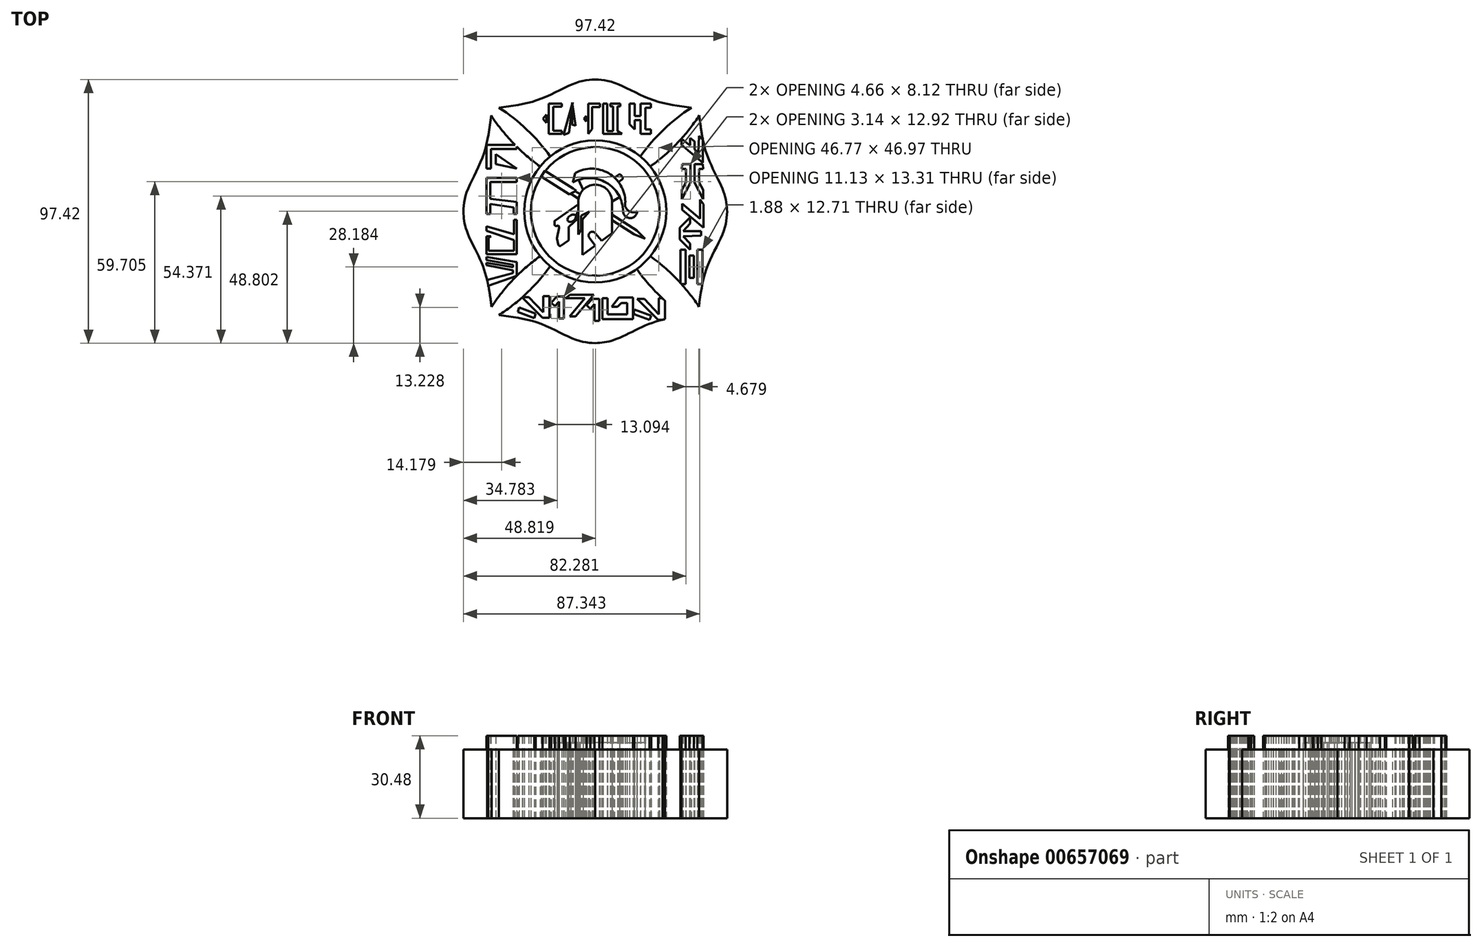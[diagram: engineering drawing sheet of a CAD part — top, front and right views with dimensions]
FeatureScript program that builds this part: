
annotation { "Feature Type Name" : "Feature", "Feature Type Description" : "" }
export const myFeature = defineFeature(function(context is Context, id is Id, definition is map)
    precondition{}
    {
        {
            var Q0;
            Q0=qCreatedBy(makeId("Top.planeOp"),FACE);
            var sketch = newSketch(context, id + "F0", { "sketchPlane" : qUnion([Q0])});
            skCircle(sketch, "E0", {"center": v(0, 0) * mm, "radius": 26.23 * mm});
            skCircle(sketch, "E1", {"center": v(0, 0) * mm, "radius": 23.74 * mm});
            skArc(sketch, "E2", {"start": v(35.51, 38.32) * mm, "mid": v(25.23, 30.18) * mm, "end": v(16.63, 20.3) * mm});
            skArc(sketch, "E3.MirrorCS", {"start": v(38.41, 35.41) * mm, "mid": v(30.25, 25.15) * mm, "end": v(20.34, 16.57) * mm});
            skArc(sketch, "E4.MirrorCS", {"start": v(-35.51, 38.32) * mm, "mid": v(-25.23, 30.18) * mm, "end": v(-16.63, 20.3) * mm});
            skArc(sketch, "E5.MirrorCS", {"start": v(-38.41, 35.41) * mm, "mid": v(-30.25, 25.15) * mm, "end": v(-20.34, 16.57) * mm});
            skArc(sketch, "E6.MirrorCS", {"start": v(-35.51, -38.32) * mm, "mid": v(-25.23, -30.18) * mm, "end": v(-16.63, -20.3) * mm});
            skArc(sketch, "E7.MirrorCS", {"start": v(-38.41, -35.41) * mm, "mid": v(-30.25, -25.15) * mm, "end": v(-20.34, -16.57) * mm});
            skArc(sketch, "E8.MirrorCS", {"start": v(38.41, -35.41) * mm, "mid": v(30.25, -25.15) * mm, "end": v(20.34, -16.57) * mm});
            skFitSpline(sketch, "E9", {"points": [v(-35.51, 38.32) * mm, v(-20.45, 41.42) * mm, v(-6.98, 47.51) * mm, v(0, 48.72) * mm], "startDerivative": vector(40.3, 5.04) * mm, "endDerivative": vector(25.56, 1.65) * mm});
            skFitSpline(sketch, "E10.MirrorCS", {"points": [v(35.51, 38.32) * mm, v(20.45, 41.42) * mm, v(6.98, 47.51) * mm, v(0, 48.72) * mm], "startDerivative": vector(-40.3, 5.04) * mm, "endDerivative": vector(-25.56, 1.65) * mm});
            skFitSpline(sketch, "E11.MirrorCS", {"points": [v(38.41, 35.41) * mm, v(41.47, 20.34) * mm, v(47.53, 6.86) * mm, v(48.72, -0.14) * mm], "startDerivative": vector(4.94, -40.31) * mm, "endDerivative": vector(1.58, -25.56) * mm});
            skFitSpline(sketch, "E12.MirrorCS", {"points": [v(38.23, -35.61) * mm, v(41.37, -20.55) * mm, v(47.5, -7.1) * mm, v(48.72, -0.12) * mm], "startDerivative": vector(5.15, 40.29) * mm, "endDerivative": vector(1.72, 25.55) * mm});
            skArc(sketch, "E13.MirrorCS", {"start": v(34.27, -39.56) * mm, "mid": v(24, -31.4) * mm, "end": v(15.43, -21.48) * mm});
            skFitSpline(sketch, "E14.MirrorCS", {"points": [v(35.51, -38.32) * mm, v(20.45, -41.42) * mm, v(6.98, -47.51) * mm, v(0, -48.72) * mm], "startDerivative": vector(-40.3, -5.04) * mm, "endDerivative": vector(-25.56, -1.65) * mm});
            skFitSpline(sketch, "E15.MirrorCS", {"points": [v(-35.51, -38.32) * mm, v(-20.45, -41.42) * mm, v(-6.98, -47.51) * mm, v(0, -48.72) * mm], "startDerivative": vector(40.3, -5.04) * mm, "endDerivative": vector(25.56, -1.65) * mm});
            skFitSpline(sketch, "E16.MirrorCS", {"points": [v(-38.23, -35.61) * mm, v(-41.37, -20.55) * mm, v(-47.5, -7.1) * mm, v(-48.72, -0.12) * mm], "startDerivative": vector(-5.15, 40.29) * mm, "endDerivative": vector(-1.72, 25.55) * mm});
            skFitSpline(sketch, "E17.MirrorCS", {"points": [v(-38.41, 35.41) * mm, v(-41.47, 20.34) * mm, v(-47.53, 6.86) * mm, v(-48.72, -0.14) * mm], "startDerivative": vector(-4.94, -40.31) * mm, "endDerivative": vector(-1.58, -25.56) * mm});
            skLineSegment(sketch, "E18.left", {"start": v(-6.25, 3.57) * mm, "end": v(-6.25, -8.57) * mm});
            skLineSegment(sketch, "E18.right", {"start": v(6.25, 3.57) * mm, "end": v(6.25, -8.06) * mm});
            skPoint(sketch, "E18.middle", {"position": v(0, -8.06) * mm});
            skArc(sketch, "E19", {"start": v(6.25, 3.57) * mm, "mid": v(0, 9.82) * mm, "end": v(-6.25, 3.57) * mm});
            skLineSegment(sketch, "E20", {"start": v(-4.67, -16.13) * mm, "end": v(0, -12.68) * mm});
            skLineSegment(sketch, "E21", {"start": v(2.37, -10.93) * mm, "end": v(0, -8.06) * mm});
            skLineSegment(sketch, "E22", {"start": v(0, -12.68) * mm, "end": v(-2.14, -9.78) * mm});
            skArc(sketch, "E23", {"start": v(0, -8.06) * mm, "mid": v(-1.93, -7.85) * mm, "end": v(-2.14, -9.78) * mm});
            skPoint(sketch, "E23.third.point", {"position": v(0, -9.78) * mm});
            skLineSegment(sketch, "E24.trimOffspring", {"start": v(2.37, -10.93) * mm, "end": v(6.25, -8.06) * mm});
            skPoint(sketch, "E18.top.end.orphan", {"position": v(6.25, -19.7) * mm});
            skPoint(sketch, "E25.orphan", {"position": v(-6.25, -19.7) * mm});
            skArc(sketch, "E26", {"start": v(11.12, 3.49) * mm, "mid": v(4.91, 14.1) * mm, "end": v(-7.38, 14.17) * mm});
            skArc(sketch, "E27", {"start": v(10.28, 0.03) * mm, "mid": v(4.07, 10.64) * mm, "end": v(-8.22, 10.7) * mm});
            skLineSegment(sketch, "E28", {"start": v(-8.22, 10.7) * mm, "end": v(-7.38, 14.17) * mm});
            skArc(sketch, "E29", {"start": v(11.12, 3.49) * mm, "mid": v(12.15, 0.3) * mm, "end": v(15.48, 0.03) * mm});
            skArc(sketch, "E30", {"start": v(10.28, 0.03) * mm, "mid": v(12.88, -2.5) * mm, "end": v(15.48, 0.03) * mm});
            skLineSegment(sketch, "E31", {"start": v(15.43, -21.48) * mm, "end": v(15.3, -21.3) * mm});
            skLineSegment(sketch, "E32", {"start": v(-4.67, -16.13) * mm, "end": v(-4.67, -2.97) * mm});
            skLineSegment(sketch, "E33", {"start": v(-4.67, -2.97) * mm, "end": v(-2.14, -0.12) * mm});
            skLineSegment(sketch, "E34", {"start": v(-2.14, -0.12) * mm, "end": v(-5.26, -1.55) * mm});
            skPoint(sketch, "E34.endSnap0", {"position": v(-3.4, -1.55) * mm});
            skLineSegment(sketch, "E35", {"start": v(-5.26, -1.55) * mm, "end": v(-5.26, -6.86) * mm});
            skPoint(sketch, "E35.endSnap0", {"position": v(-6.25, -6.86) * mm});
            skLineSegment(sketch, "E36", {"start": v(-5.26, -6.86) * mm, "end": v(-6.25, -8.57) * mm});
            skPoint(sketch, "E37.orphan", {"position": v(-6.25, -17.3) * mm});
            skLineSegment(sketch, "E38", {"start": v(-4.46, 7.95) * mm, "end": v(-6.14, 11.64) * mm});
            skLineSegment(sketch, "E39", {"start": v(6.25, 3.57) * mm, "end": v(9.04, 5.3) * mm});
            skLineSegment(sketch, "E40.bottom", {"start": v(-12.4, 39.78) * mm, "end": v(-17.13, 39.78) * mm});
            skLineSegment(sketch, "E40.top", {"start": v(-12.4, 38.6) * mm, "end": v(-15.49, 38.6) * mm});
            skLineSegment(sketch, "E40.left", {"start": v(-12.4, 39.78) * mm, "end": v(-12.4, 38.6) * mm});
            skLineSegment(sketch, "E40.right", {"start": v(-17.13, 39.78) * mm, "end": v(-17.13, 38.6) * mm});
            skLineSegment(sketch, "E41.bottom", {"start": v(-17.13, 39.78) * mm, "end": v(-15.49, 39.78) * mm});
            skLineSegment(sketch, "E41.left", {"start": v(-17.13, 39.78) * mm, "end": v(-17.13, 34.21) * mm});
            skLineSegment(sketch, "E41.right", {"start": v(-15.49, 38.6) * mm, "end": v(-15.49, 34.21) * mm});
            skLineSegment(sketch, "E42.bottom", {"start": v(-2.52, 39.78) * mm, "end": v(-1.13, 39.78) * mm});
            skLineSegment(sketch, "E42.left", {"start": v(-2.52, 39.78) * mm, "end": v(-2.52, 34.21) * mm});
            skLineSegment(sketch, "E42.right", {"start": v(-1.13, 38.54) * mm, "end": v(-1.13, 34.21) * mm});
            skLineSegment(sketch, "E43.bottom", {"start": v(-2.52, 39.78) * mm, "end": v(1.82, 39.78) * mm});
            skLineSegment(sketch, "E43.top", {"start": v(-1.13, 38.54) * mm, "end": v(1.82, 38.54) * mm});
            skLineSegment(sketch, "E43.left", {"start": v(-2.52, 39.78) * mm, "end": v(-2.52, 38.54) * mm});
            skLineSegment(sketch, "E43.right", {"start": v(1.82, 39.78) * mm, "end": v(1.82, 38.54) * mm});
            skLineSegment(sketch, "E44", {"start": v(-8.28, 40.2) * mm, "end": v(-8.4, 39.75) * mm});
            skLineSegment(sketch, "E45", {"start": v(-11.7, 28.2) * mm, "end": v(-9.65, 28.98) * mm});
            skLineSegment(sketch, "E46", {"start": v(-9.65, 28.98) * mm, "end": v(-8.48, 38.58) * mm});
            skLineSegment(sketch, "E47", {"start": v(-8.48, 40.2) * mm, "end": v(-8.48, 39.51) * mm});
            skLineSegment(sketch, "E48", {"start": v(-8.48, 32.05) * mm, "end": v(-7.25, 31.7) * mm});
            skLineSegment(sketch, "E49", {"start": v(-7.25, 31.7) * mm, "end": v(-8.37, 39.46) * mm});
            skLineSegment(sketch, "E50.MirrorCS", {"start": v(-12.4, 28.65) * mm, "end": v(-17.13, 28.65) * mm});
            skLineSegment(sketch, "E51.MirrorCS", {"start": v(-12.4, 29.82) * mm, "end": v(-15.49, 29.82) * mm});
            skLineSegment(sketch, "E52.MirrorCS", {"start": v(-12.4, 28.65) * mm, "end": v(-12.4, 29.82) * mm});
            skLineSegment(sketch, "E53.MirrorCS", {"start": v(-17.13, 28.65) * mm, "end": v(-17.13, 34.21) * mm});
            skLineSegment(sketch, "E54.MirrorCS", {"start": v(-15.49, 29.82) * mm, "end": v(-15.49, 34.21) * mm});
            skLineSegment(sketch, "E55.MirrorCS", {"start": v(-2.52, 28.65) * mm, "end": v(-2.52, 34.21) * mm});
            skLineSegment(sketch, "E56.MirrorCS", {"start": v(-1.13, 30.44) * mm, "end": v(-1.13, 34.21) * mm});
            skLineSegment(sketch, "E57", {"start": v(-2.52, 28.65) * mm, "end": v(-1.13, 30.44) * mm});
            skPoint(sketch, "E58.orphan", {"position": v(-1.13, 28.65) * mm});
            skPoint(sketch, "E59.orphan", {"position": v(10.7, 28.65) * mm});
            skPoint(sketch, "E60.orphan", {"position": v(10.28, 29.44) * mm});
            skLineSegment(sketch, "E61", {"start": v(-3.29, 35.2) * mm, "end": v(-3.29, 34.21) * mm});
            skPoint(sketch, "E61.endSnap0", {"position": v(-18.03, 34.21) * mm});
            skLineSegment(sketch, "E62", {"start": v(-4.27, 34.21) * mm, "end": v(-3.29, 35.2) * mm});
            skLineSegment(sketch, "E63.MirrorCS", {"start": v(-3.29, 33.23) * mm, "end": v(-3.29, 34.21) * mm});
            skLineSegment(sketch, "E64.MirrorCS", {"start": v(-4.27, 34.21) * mm, "end": v(-3.29, 33.23) * mm});
            skLineSegment(sketch, "E65", {"start": v(-18.03, 35.71) * mm, "end": v(-19.33, 34.21) * mm});
            skLineSegment(sketch, "E66", {"start": v(-18.03, 34.21) * mm, "end": v(-18.03, 35.71) * mm});
            skLineSegment(sketch, "E67", {"start": v(-18.03, 34.21) * mm, "end": v(-18.03, 32.71) * mm});
            skLineSegment(sketch, "E68", {"start": v(-18.03, 32.71) * mm, "end": v(-19.33, 34.21) * mm});
            skLineSegment(sketch, "E69.bottom", {"start": v(2.96, 39.78) * mm, "end": v(4.44, 39.78) * mm});
            skLineSegment(sketch, "E69.top", {"start": v(2.96, 28.65) * mm, "end": v(4.44, 28.65) * mm});
            skLineSegment(sketch, "E69.left", {"start": v(2.96, 39.78) * mm, "end": v(2.96, 28.65) * mm});
            skLineSegment(sketch, "E69.right", {"start": v(4.44, 39.78) * mm, "end": v(4.44, 29.7) * mm});
            skLineSegment(sketch, "E70.bottom", {"start": v(2.96, 28.65) * mm, "end": v(8.18, 28.65) * mm});
            skLineSegment(sketch, "E70.top", {"start": v(4.44, 29.7) * mm, "end": v(6.61, 29.7) * mm});
            skLineSegment(sketch, "E70.left", {"start": v(2.96, 28.65) * mm, "end": v(2.96, 29.7) * mm});
            skLineSegment(sketch, "E71.bottom", {"start": v(8.18, 28.65) * mm, "end": v(6.61, 28.65) * mm});
            skLineSegment(sketch, "E71.top", {"start": v(8.18, 39.78) * mm, "end": v(6.61, 39.78) * mm});
            skLineSegment(sketch, "E71.left", {"start": v(8.18, 29.7) * mm, "end": v(8.18, 38.83) * mm});
            skLineSegment(sketch, "E71.right", {"start": v(6.61, 29.7) * mm, "end": v(6.61, 38.83) * mm});
            skLineSegment(sketch, "E72.bottom", {"start": v(5.53, 39.78) * mm, "end": v(9.3, 39.78) * mm});
            skLineSegment(sketch, "E72.top", {"start": v(5.53, 38.83) * mm, "end": v(6.61, 38.83) * mm});
            skLineSegment(sketch, "E72.left", {"start": v(5.53, 39.78) * mm, "end": v(5.53, 38.83) * mm});
            skLineSegment(sketch, "E72.right", {"start": v(9.3, 39.78) * mm, "end": v(9.3, 38.83) * mm});
            skLineSegment(sketch, "E73", {"start": v(8.18, 29.7) * mm, "end": v(9.87, 28.65) * mm});
            skLineSegment(sketch, "E74", {"start": v(9.87, 28.65) * mm, "end": v(8.18, 28.65) * mm});
            skLineSegment(sketch, "E75.trimOffspring", {"start": v(8.18, 38.83) * mm, "end": v(9.3, 38.83) * mm});
            skLineSegment(sketch, "E76", {"start": v(12.66, 39.78) * mm, "end": v(14.62, 39.78) * mm});
            skLineSegment(sketch, "E77.left", {"start": v(12.66, 39.78) * mm, "end": v(12.66, 32.13) * mm});
            skLineSegment(sketch, "E77.right", {"start": v(14.62, 39.78) * mm, "end": v(14.62, 35.22) * mm});
            skLineSegment(sketch, "E78.bottom", {"start": v(14.62, 35.22) * mm, "end": v(16.76, 35.22) * mm});
            skLineSegment(sketch, "E78.top", {"start": v(14.62, 33.67) * mm, "end": v(16.76, 33.67) * mm});
            skLineSegment(sketch, "E78.left", {"start": v(12.66, 35.22) * mm, "end": v(12.66, 33.67) * mm});
            skLineSegment(sketch, "E79.bottom", {"start": v(16.76, 39.78) * mm, "end": v(18.48, 39.78) * mm});
            skLineSegment(sketch, "E79.top", {"start": v(16.76, 28.65) * mm, "end": v(18.48, 28.65) * mm});
            skLineSegment(sketch, "E79.left", {"start": v(16.76, 39.78) * mm, "end": v(16.76, 35.22) * mm});
            skLineSegment(sketch, "E79.right", {"start": v(18.48, 38.24) * mm, "end": v(18.48, 30.3) * mm});
            skLineSegment(sketch, "E80.bottom", {"start": v(16.76, 39.78) * mm, "end": v(20.61, 39.78) * mm});
            skLineSegment(sketch, "E80.top", {"start": v(18.48, 38.24) * mm, "end": v(20.61, 38.24) * mm});
            skLineSegment(sketch, "E80.left", {"start": v(16.76, 39.78) * mm, "end": v(16.76, 38.24) * mm});
            skLineSegment(sketch, "E80.right", {"start": v(20.61, 39.78) * mm, "end": v(20.61, 38.24) * mm});
            skLineSegment(sketch, "E81.bottom", {"start": v(16.76, 28.65) * mm, "end": v(20.61, 28.65) * mm});
            skLineSegment(sketch, "E81.top", {"start": v(18.48, 30.3) * mm, "end": v(20.61, 30.3) * mm});
            skLineSegment(sketch, "E81.left", {"start": v(16.76, 28.65) * mm, "end": v(16.76, 30.3) * mm});
            skLineSegment(sketch, "E81.right", {"start": v(20.61, 28.65) * mm, "end": v(20.61, 30.3) * mm});
            skLineSegment(sketch, "E82.trimOffspring", {"start": v(18.48, 28.65) * mm, "end": v(20.61, 28.65) * mm});
            skLineSegment(sketch, "E83", {"start": v(12.66, 32.13) * mm, "end": v(14.62, 30.23) * mm});
            skLineSegment(sketch, "E84.trimOffspring", {"start": v(16.76, 33.67) * mm, "end": v(16.76, 28.65) * mm});
            skLineSegment(sketch, "E85.trimOffspring", {"start": v(14.62, 33.67) * mm, "end": v(14.62, 30.23) * mm});
            skLineSegment(sketch, "E86.trimOffspring", {"start": v(-8.4, 39.75) * mm, "end": v(-8.48, 40.2) * mm});
            skLineSegment(sketch, "E87.trimOffspring", {"start": v(-8.48, 39.51) * mm, "end": v(-11.7, 28.2) * mm});
            skLineSegment(sketch, "E88.trimOffspring", {"start": v(-8.37, 39.46) * mm, "end": v(-8.28, 40.2) * mm});
            skLineSegment(sketch, "E89.trimOffspring", {"start": v(-8.48, 38.58) * mm, "end": v(-8.48, 32.05) * mm});
            skLineSegment(sketch, "E90", {"start": v(-28.97, -18.8) * mm, "end": v(-40.1, -16.82) * mm});
            skLineSegment(sketch, "E91", {"start": v(-40.1, -16.82) * mm, "end": v(-40.1, -18.04) * mm});
            skLineSegment(sketch, "E92", {"start": v(-40.1, -18.04) * mm, "end": v(-30.4, -19.76) * mm});
            skLineSegment(sketch, "E93", {"start": v(-30.4, -19.76) * mm, "end": v(-30.4, -20.72) * mm});
            skLineSegment(sketch, "E94", {"start": v(-30.4, -20.72) * mm, "end": v(-40.1, -19) * mm});
            skLineSegment(sketch, "E95", {"start": v(-40.1, -19) * mm, "end": v(-40.1, -19.9) * mm});
            skLineSegment(sketch, "E96", {"start": v(-40.1, -19.9) * mm, "end": v(-30.32, -21.8) * mm});
            skLineSegment(sketch, "E97", {"start": v(-30.32, -21.8) * mm, "end": v(-30.32, -22.87) * mm});
            skLineSegment(sketch, "E98", {"start": v(-30.32, -22.87) * mm, "end": v(-40.1, -25.47) * mm});
            skLineSegment(sketch, "E99", {"start": v(-40.1, -25.47) * mm, "end": v(-40.1, -27.73) * mm});
            skLineSegment(sketch, "E100", {"start": v(-40.1, -27.73) * mm, "end": v(-28.97, -23.85) * mm});
            skLineSegment(sketch, "E101", {"start": v(-28.97, -23.85) * mm, "end": v(-28.97, -18.8) * mm});
            skLineSegment(sketch, "E102.bottom", {"start": v(-40.1, -15.83) * mm, "end": v(-40.1, -14.56) * mm});
            skLineSegment(sketch, "E102.left", {"start": v(-40.1, -15.83) * mm, "end": v(-28.97, -15.83) * mm});
            skLineSegment(sketch, "E102.right", {"start": v(-39.41, -14.56) * mm, "end": v(-30.02, -14.56) * mm});
            skLineSegment(sketch, "E103.bottom", {"start": v(-28.97, -15.83) * mm, "end": v(-28.97, -3.12) * mm});
            skLineSegment(sketch, "E103.top", {"start": v(-30.02, -14.56) * mm, "end": v(-30.02, -10.64) * mm});
            skLineSegment(sketch, "E103.left", {"start": v(-28.97, -15.83) * mm, "end": v(-30.02, -15.83) * mm});
            skLineSegment(sketch, "E103.right", {"start": v(-28.97, -3.12) * mm, "end": v(-30.02, -3.12) * mm});
            skLineSegment(sketch, "E104.left", {"start": v(-38.1, -6.34) * mm, "end": v(-38.11, -6.34) * mm});
            skLineSegment(sketch, "E104.right", {"start": v(-38.1, -5.52) * mm, "end": v(-38.11, -5.52) * mm});
            skLineSegment(sketch, "E105.bottom", {"start": v(-40.1, -15.83) * mm, "end": v(-40.1, -9.27) * mm});
            skLineSegment(sketch, "E105.top", {"start": v(-39.41, -14.56) * mm, "end": v(-39.41, -9.91) * mm});
            skLineSegment(sketch, "E105.left", {"start": v(-40.1, -15.83) * mm, "end": v(-39.41, -15.83) * mm});
            skLineSegment(sketch, "E105.right", {"start": v(-40.1, -9.27) * mm, "end": v(-39.41, -9.27) * mm});
            skLineSegment(sketch, "E106", {"start": v(-40.1, -9.27) * mm, "end": v(-38.43, -9.27) * mm});
            skPoint(sketch, "E106.endSnap0", {"position": v(-39.75, -9.27) * mm});
            skLineSegment(sketch, "E107", {"start": v(-38.43, -9.27) * mm, "end": v(-39.41, -9.91) * mm});
            skLineSegment(sketch, "E108", {"start": v(-30.02, -10.64) * mm, "end": v(-40.1, -7.24) * mm});
            skLineSegment(sketch, "E109", {"start": v(-40.1, -7.24) * mm, "end": v(-40.1, -5.52) * mm});
            skLineSegment(sketch, "E110", {"start": v(-40.1, -5.52) * mm, "end": v(-30.02, -8.5) * mm});
            skLineSegment(sketch, "E111.bottom", {"start": v(-28.97, -0.92) * mm, "end": v(-28.97, 3.44) * mm});
            skLineSegment(sketch, "E111.top", {"start": v(-30.13, -0.92) * mm, "end": v(-30.13, 1.44) * mm});
            skLineSegment(sketch, "E111.left", {"start": v(-28.97, -0.92) * mm, "end": v(-30.13, -0.92) * mm});
            skLineSegment(sketch, "E111.right", {"start": v(-28.97, 3.44) * mm, "end": v(-30.13, 3.44) * mm});
            skLineSegment(sketch, "E112", {"start": v(-30.13, 1.44) * mm, "end": v(-38.78, 2.72) * mm});
            skLineSegment(sketch, "E113", {"start": v(-40.1, 2.92) * mm, "end": v(-40.1, 4.72) * mm});
            skLineSegment(sketch, "E114", {"start": v(-38.78, 4.57) * mm, "end": v(-28.97, 3.44) * mm});
            skLineSegment(sketch, "E115.bottom", {"start": v(-40.1, -1) * mm, "end": v(-40.1, 12.32) * mm});
            skLineSegment(sketch, "E115.top", {"start": v(-38.78, -1) * mm, "end": v(-38.78, 2.72) * mm});
            skLineSegment(sketch, "E115.left", {"start": v(-40.1, -1) * mm, "end": v(-38.78, -1) * mm});
            skLineSegment(sketch, "E115.right", {"start": v(-40.1, 12.32) * mm, "end": v(-38.78, 12.32) * mm});
            skLineSegment(sketch, "E116.bottom", {"start": v(-40.1, 12.32) * mm, "end": v(-40.1, 10.89) * mm});
            skLineSegment(sketch, "E116.top", {"start": v(-28.97, 12.32) * mm, "end": v(-28.97, 10.89) * mm});
            skLineSegment(sketch, "E116.left", {"start": v(-40.1, 12.32) * mm, "end": v(-28.97, 12.32) * mm});
            skLineSegment(sketch, "E116.right", {"start": v(-38.78, 10.89) * mm, "end": v(-28.97, 10.89) * mm});
            skLineSegment(sketch, "E117", {"start": v(-40.1, 15.79) * mm, "end": v(-40.1, 24.5) * mm});
            skLineSegment(sketch, "E118.top", {"start": v(-38.46, 15.79) * mm, "end": v(-38.46, 22.98) * mm});
            skLineSegment(sketch, "E118.left", {"start": v(-40.1, 15.79) * mm, "end": v(-38.46, 15.79) * mm});
            skLineSegment(sketch, "E118.right", {"start": v(-40.1, 24.5) * mm, "end": v(-38.46, 24.5) * mm});
            skLineSegment(sketch, "E119.bottom", {"start": v(-40.1, 24.5) * mm, "end": v(-40.1, 22.98) * mm});
            skLineSegment(sketch, "E119.top", {"start": v(-29, 24.5) * mm, "end": v(-29, 22.98) * mm});
            skLineSegment(sketch, "E119.left", {"start": v(-40.1, 24.5) * mm, "end": v(-29, 24.5) * mm});
            skLineSegment(sketch, "E119.right", {"start": v(-38.46, 22.98) * mm, "end": v(-29, 22.98) * mm});
            skLineSegment(sketch, "E120", {"start": v(-28.97, 15.79) * mm, "end": v(-36.7, 17.48) * mm});
            skLineSegment(sketch, "E121", {"start": v(-36.7, 17.48) * mm, "end": v(-36.7, 21.15) * mm});
            skLineSegment(sketch, "E122", {"start": v(-36.7, 21.15) * mm, "end": v(-28.97, 15.79) * mm});
            skLineSegment(sketch, "E123.trimOffspring", {"start": v(-38.78, 4.57) * mm, "end": v(-38.78, 10.89) * mm});
            skLineSegment(sketch, "E124.trimOffspring", {"start": v(-30.02, -8.5) * mm, "end": v(-30.02, -3.12) * mm});
            skPoint(sketch, "E125.orphan", {"position": v(-40.1, -23.85) * mm});
            skPoint(sketch, "E126.orphan", {"position": v(-28.97, 1.26) * mm});
            skLineSegment(sketch, "E127.bottom", {"start": v(-19.94, 12.89) * mm, "end": v(-9.54, 6.25) * mm});
            skLineSegment(sketch, "E127.top", {"start": v(-18.56, 15.04) * mm, "end": v(-8.17, 8.4) * mm});
            skLineSegment(sketch, "E127.left", {"start": v(-19.94, 12.89) * mm, "end": v(-18.56, 15.04) * mm});
            skLineSegment(sketch, "E127.right", {"start": v(-9.54, 6.25) * mm, "end": v(-8.17, 8.4) * mm});
            skLineSegment(sketch, "E128", {"start": v(-5.9, 6.52) * mm, "end": v(-5.6, 6.34) * mm});
            skLineSegment(sketch, "E129", {"start": v(-7.93, 5.76) * mm, "end": v(-6.16, 4.63) * mm});
            skLineSegment(sketch, "E130", {"start": v(14.39, -8.5) * mm, "end": v(18.41, -10.1) * mm});
            skPoint(sketch, "E130.endSnap0", {"position": v(-81.83, -16.44) * mm});
            skLineSegment(sketch, "E131", {"start": v(18.41, -10.1) * mm, "end": v(15.32, -7.03) * mm});
            skLineSegment(sketch, "E132.0", {"start": v(14.39, -8.5) * mm, "end": v(15.32, -7.03) * mm, "construction": true});
            skLineSegment(sketch, "E133.trimOffspring", {"start": v(6.25, -1.24) * mm, "end": v(15.32, -7.03) * mm});
            skLineSegment(sketch, "E134.trimOffspring", {"start": v(6.25, -3.3) * mm, "end": v(14.39, -8.5) * mm});
            skLineSegment(sketch, "E135", {"start": v(-9.54, 6.25) * mm, "end": v(-7.04, 7.6) * mm});
            skPoint(sketch, "E135.endSnap0", {"position": v(-7.04, 5.2) * mm});
            skLineSegment(sketch, "E136", {"start": v(-7.04, 7.6) * mm, "end": v(-8.17, 8.4) * mm});
            skLineSegment(sketch, "E137", {"start": v(-5.9, 6.52) * mm, "end": v(-7.34, 7.44) * mm});
            skLineSegment(sketch, "E138", {"start": v(-7.93, 5.76) * mm, "end": v(-9.08, 6.5) * mm});
            skLineSegment(sketch, "E139", {"start": v(-9.76, -10.38) * mm, "end": v(-9.76, -5.95) * mm});
            skLineSegment(sketch, "E140", {"start": v(-9.56, -5.5) * mm, "end": v(-6.53, -2.75) * mm});
            skLineSegment(sketch, "E141", {"start": v(-6.35, -2.14) * mm, "end": v(-6.69, -0.96) * mm});
            skLineSegment(sketch, "E142", {"start": v(-6.46, -0.3) * mm, "end": v(-6.25, -0.16) * mm});
            skLineSegment(sketch, "E143", {"start": v(-10.01, -10.87) * mm, "end": v(-12.63, -12.7) * mm});
            skLineSegment(sketch, "E144", {"start": v(-13.55, -12.37) * mm, "end": v(-14.15, -10.12) * mm});
            skLineSegment(sketch, "E145", {"start": v(-14.15, -9.83) * mm, "end": v(-13.33, -6.24) * mm});
            skLineSegment(sketch, "E146", {"start": v(-13.33, -5.94) * mm, "end": v(-13.56, -5.15) * mm});
            skLineSegment(sketch, "E147", {"start": v(-13.56, -5.15) * mm, "end": v(-14.29, -5.36) * mm});
            skLineSegment(sketch, "E148", {"start": v(-15.05, -4.78) * mm, "end": v(-15.05, -3.9) * mm});
            skLineSegment(sketch, "E149", {"start": v(-14.8, -3.4) * mm, "end": v(-6.25, 2.58) * mm});
            skLineSegment(sketch, "E150", {"start": v(8.64, 10.79) * mm, "end": v(9.96, 11.84) * mm});
            skLineSegment(sketch, "E151", {"start": v(10.06, 12.68) * mm, "end": v(9.46, 13.43) * mm});
            skLineSegment(sketch, "E152", {"start": v(8.65, 13.55) * mm, "end": v(7.08, 12.46) * mm});
            skEllipse(sketch, "E153", {"center": v(-8.66, -2.52) * mm, "majorRadius": 1.77 * mm, "minorRadius": 1.1 * mm, "majorAxis": v(0.82, 0.57)});
            skPoint(sketch, "E154.visualSharp", {"position": v(-13.33, -13.2) * mm});
            skArc(sketch, "E154.filletArc", {"start": v(-13.55, -12.37) * mm, "mid": v(-13.18, -12.78) * mm, "end": v(-12.63, -12.7) * mm});
            skPoint(sketch, "E155.visualSharp", {"position": v(-9.76, -10.7) * mm});
            skArc(sketch, "E155.filletArc", {"start": v(-10.01, -10.87) * mm, "mid": v(-9.83, -10.66) * mm, "end": v(-9.76, -10.38) * mm});
            skPoint(sketch, "E156.visualSharp", {"position": v(-9.76, -5.69) * mm});
            skArc(sketch, "E156.filletArc", {"start": v(-9.56, -5.5) * mm, "mid": v(-9.7, -5.7) * mm, "end": v(-9.76, -5.95) * mm});
            skPoint(sketch, "E157.visualSharp", {"position": v(-6.25, -2.5) * mm});
            skArc(sketch, "E157.filletArc", {"start": v(-6.53, -2.75) * mm, "mid": v(-6.35, -2.47) * mm, "end": v(-6.35, -2.14) * mm});
            skPoint(sketch, "E158.visualSharp", {"position": v(-6.8, -0.54) * mm});
            skArc(sketch, "E158.filletArc", {"start": v(-6.46, -0.3) * mm, "mid": v(-6.68, -0.6) * mm, "end": v(-6.69, -0.96) * mm});
            skPoint(sketch, "E159.visualSharp", {"position": v(-14.18, -9.98) * mm});
            skArc(sketch, "E159.filletArc", {"start": v(-14.15, -9.83) * mm, "mid": v(-14.17, -9.98) * mm, "end": v(-14.15, -10.12) * mm});
            skPoint(sketch, "E160.visualSharp", {"position": v(-13.3, -6.09) * mm});
            skArc(sketch, "E160.filletArc", {"start": v(-13.33, -6.24) * mm, "mid": v(-13.31, -6.09) * mm, "end": v(-13.33, -5.94) * mm});
            skPoint(sketch, "E161.visualSharp", {"position": v(-15.05, -5.58) * mm});
            skArc(sketch, "E161.filletArc", {"start": v(-15.05, -4.78) * mm, "mid": v(-14.81, -5.26) * mm, "end": v(-14.29, -5.36) * mm});
            skPoint(sketch, "E162.visualSharp", {"position": v(-15.05, -3.59) * mm});
            skArc(sketch, "E162.filletArc", {"start": v(-14.8, -3.4) * mm, "mid": v(-14.98, -3.62) * mm, "end": v(-15.05, -3.9) * mm});
            skPoint(sketch, "E163.visualSharp", {"position": v(10.43, 12.21) * mm});
            skArc(sketch, "E163.filletArc", {"start": v(9.96, 11.84) * mm, "mid": v(10.19, 12.24) * mm, "end": v(10.06, 12.68) * mm});
            skPoint(sketch, "E164.visualSharp", {"position": v(9.11, 13.88) * mm});
            skArc(sketch, "E164.filletArc", {"start": v(9.46, 13.43) * mm, "mid": v(9.08, 13.65) * mm, "end": v(8.65, 13.55) * mm});
            skLineSegment(sketch, "E165", {"start": v(38.28, 27.89) * mm, "end": v(39.78, 26.46) * mm});
            skLineSegment(sketch, "E166", {"start": v(39.78, 26.46) * mm, "end": v(39.78, 17.96) * mm});
            skLineSegment(sketch, "E167", {"start": v(39.78, 17.96) * mm, "end": v(31.81, 24.58) * mm});
            skLineSegment(sketch, "E168", {"start": v(31.81, 24.58) * mm, "end": v(31.81, 26.84) * mm});
            skLineSegment(sketch, "E169", {"start": v(31.81, 26.84) * mm, "end": v(35.04, 24.28) * mm});
            skLineSegment(sketch, "E170", {"start": v(35.04, 24.28) * mm, "end": v(35.04, 27.06) * mm});
            skLineSegment(sketch, "E171", {"start": v(35.04, 27.06) * mm, "end": v(36.62, 25.86) * mm});
            skLineSegment(sketch, "E172", {"start": v(36.62, 25.86) * mm, "end": v(36.62, 22.93) * mm});
            skLineSegment(sketch, "E173", {"start": v(36.62, 22.93) * mm, "end": v(38.05, 21.57) * mm});
            skLineSegment(sketch, "E174", {"start": v(38.05, 21.57) * mm, "end": v(38.28, 27.89) * mm});
            skLineSegment(sketch, "E175", {"start": v(39.77, 17.46) * mm, "end": v(36.68, 17.46) * mm});
            skLineSegment(sketch, "E176", {"start": v(36.68, 17.46) * mm, "end": v(36.68, 10.57) * mm});
            skLineSegment(sketch, "E177", {"start": v(36.68, 10.57) * mm, "end": v(39.82, 4.53) * mm});
            skLineSegment(sketch, "E178", {"start": v(39.82, 4.53) * mm, "end": v(39.82, 7.86) * mm});
            skLineSegment(sketch, "E179", {"start": v(39.82, 7.86) * mm, "end": v(38.34, 10.7) * mm});
            skLineSegment(sketch, "E180", {"start": v(38.34, 10.7) * mm, "end": v(38.34, 15.65) * mm});
            skLineSegment(sketch, "E181", {"start": v(38.34, 15.65) * mm, "end": v(39.82, 15.65) * mm});
            skLineSegment(sketch, "E182", {"start": v(39.82, 15.65) * mm, "end": v(39.77, 17.46) * mm});
            skLineSegment(sketch, "E183.MirrorCS", {"start": v(32.06, 17.46) * mm, "end": v(35.14, 17.46) * mm});
            skLineSegment(sketch, "E184.MirrorCS", {"start": v(32, 15.65) * mm, "end": v(32.06, 17.46) * mm});
            skLineSegment(sketch, "E185.MirrorCS", {"start": v(33.48, 15.65) * mm, "end": v(32, 15.65) * mm});
            skLineSegment(sketch, "E186.MirrorCS", {"start": v(35.14, 17.46) * mm, "end": v(35.14, 10.57) * mm});
            skLineSegment(sketch, "E187.MirrorCS", {"start": v(33.48, 10.7) * mm, "end": v(33.48, 15.65) * mm});
            skLineSegment(sketch, "E188.MirrorCS", {"start": v(32, 7.86) * mm, "end": v(33.48, 10.7) * mm});
            skLineSegment(sketch, "E189.MirrorCS", {"start": v(35.14, 10.57) * mm, "end": v(32, 4.53) * mm});
            skLineSegment(sketch, "E190.MirrorCS", {"start": v(32, 4.53) * mm, "end": v(32, 7.86) * mm});
            skLineSegment(sketch, "E191", {"start": v(32.06, 2.86) * mm, "end": v(32.06, 0.6) * mm});
            skLineSegment(sketch, "E192", {"start": v(32.06, 0.6) * mm, "end": v(40.03, -6.01) * mm});
            skLineSegment(sketch, "E193", {"start": v(40.03, -6.01) * mm, "end": v(40.03, 2.63) * mm});
            skLineSegment(sketch, "E194", {"start": v(40.03, 2.63) * mm, "end": v(38.7, 4.4) * mm});
            skLineSegment(sketch, "E195", {"start": v(38.7, 4.4) * mm, "end": v(38.7, -2.78) * mm});
            skLineSegment(sketch, "E196", {"start": v(38.7, -2.78) * mm, "end": v(32.06, 2.86) * mm});
            skLineSegment(sketch, "E197", {"start": v(31.2, -10.41) * mm, "end": v(31.2, -6.01) * mm});
            skLineSegment(sketch, "E198", {"start": v(31.2, -6.01) * mm, "end": v(35.04, -2.25) * mm});
            skLineSegment(sketch, "E199", {"start": v(35.04, -2.25) * mm, "end": v(35.04, -4.58) * mm});
            skLineSegment(sketch, "E200", {"start": v(35.04, -4.58) * mm, "end": v(32.48, -7.33) * mm});
            skLineSegment(sketch, "E201", {"start": v(32.48, -7.33) * mm, "end": v(39.06, -7.33) * mm});
            skLineSegment(sketch, "E202", {"start": v(39.06, -7.33) * mm, "end": v(39.06, -9.02) * mm});
            skLineSegment(sketch, "E203", {"start": v(39.06, -9.02) * mm, "end": v(32.44, -9.17) * mm});
            skLineSegment(sketch, "E204", {"start": v(32.44, -9.17) * mm, "end": v(35.04, -11.84) * mm});
            skLineSegment(sketch, "E205", {"start": v(35.04, -11.84) * mm, "end": v(35.04, -14.17) * mm});
            skLineSegment(sketch, "E206", {"start": v(35.04, -14.17) * mm, "end": v(31.2, -10.41) * mm});
            skLineSegment(sketch, "E207.bottom", {"start": v(39.57, -14.17) * mm, "end": v(39.57, -26.88) * mm});
            skLineSegment(sketch, "E207.top", {"start": v(37.7, -14.17) * mm, "end": v(37.7, -26.88) * mm});
            skLineSegment(sketch, "E207.left", {"start": v(39.57, -14.17) * mm, "end": v(37.7, -14.17) * mm});
            skLineSegment(sketch, "E207.right", {"start": v(39.57, -26.88) * mm, "end": v(37.7, -26.88) * mm});
            skLineSegment(sketch, "E208.bottom", {"start": v(36.5, -16.28) * mm, "end": v(36.5, -24.62) * mm});
            skLineSegment(sketch, "E208.top", {"start": v(34.76, -16.28) * mm, "end": v(34.76, -24.62) * mm});
            skLineSegment(sketch, "E208.left", {"start": v(36.5, -16.28) * mm, "end": v(34.76, -16.28) * mm});
            skLineSegment(sketch, "E208.right", {"start": v(36.5, -24.62) * mm, "end": v(34.76, -24.62) * mm});
            skLineSegment(sketch, "E209.bottom", {"start": v(33.33, -14.17) * mm, "end": v(33.33, -26.88) * mm});
            skLineSegment(sketch, "E209.top", {"start": v(31.45, -14.17) * mm, "end": v(31.45, -26.88) * mm});
            skLineSegment(sketch, "E209.left", {"start": v(33.33, -14.17) * mm, "end": v(31.45, -14.17) * mm});
            skLineSegment(sketch, "E209.right", {"start": v(33.33, -26.88) * mm, "end": v(31.45, -26.88) * mm});
            skLineSegment(sketch, "E210", {"start": v(-27, -31.8) * mm, "end": v(-19.4, -39.36) * mm});
            skLineSegment(sketch, "E211", {"start": v(-19.4, -39.36) * mm, "end": v(-16.9, -39.36) * mm});
            skLineSegment(sketch, "E212", {"start": v(-16.9, -39.36) * mm, "end": v(-16.9, -31.38) * mm});
            skLineSegment(sketch, "E213", {"start": v(-16.9, -31.38) * mm, "end": v(-19.18, -31.38) * mm});
            skLineSegment(sketch, "E214", {"start": v(-19.18, -31.38) * mm, "end": v(-19.18, -37.34) * mm});
            skLineSegment(sketch, "E215", {"start": v(-19.18, -37.34) * mm, "end": v(-24.5, -31.65) * mm});
            skLineSegment(sketch, "E216", {"start": v(-24.5, -31.65) * mm, "end": v(-26.81, -31.65) * mm});
            skLineSegment(sketch, "E217", {"start": v(-28.12, -35.53) * mm, "end": v(-21.95, -37.81) * mm});
            skLineSegment(sketch, "E218", {"start": v(-21.95, -37.81) * mm, "end": v(-22.53, -39.4) * mm});
            skLineSegment(sketch, "E219", {"start": v(-22.53, -39.4) * mm, "end": v(-28.62, -37.14) * mm});
            skLineSegment(sketch, "E220", {"start": v(-28.62, -37.14) * mm, "end": v(-28.12, -35.53) * mm});
            skLineSegment(sketch, "E221", {"start": v(-16.26, -33.68) * mm, "end": v(-14.08, -31.42) * mm});
            skLineSegment(sketch, "E222", {"start": v(-14.08, -31.42) * mm, "end": v(-11.6, -31.42) * mm});
            skLineSegment(sketch, "E223", {"start": v(-11.6, -31.42) * mm, "end": v(-11.6, -39.54) * mm});
            skLineSegment(sketch, "E224", {"start": v(-11.6, -39.54) * mm, "end": v(-13.33, -39.54) * mm});
            skLineSegment(sketch, "E225", {"start": v(-13.33, -39.54) * mm, "end": v(-13.33, -33.3) * mm});
            skLineSegment(sketch, "E226", {"start": v(-13.33, -33.3) * mm, "end": v(-14.9, -35.03) * mm});
            skLineSegment(sketch, "E227", {"start": v(-14.9, -35.03) * mm, "end": v(-16.26, -33.68) * mm});
            skLineSegment(sketch, "E228", {"start": v(-9.45, -38.79) * mm, "end": v(-7.2, -38.79) * mm});
            skLineSegment(sketch, "E229", {"start": v(-7.2, -38.79) * mm, "end": v(-0.58, -30.82) * mm});
            skLineSegment(sketch, "E230", {"start": v(-0.58, -30.82) * mm, "end": v(-9.23, -30.82) * mm});
            skLineSegment(sketch, "E231", {"start": v(-9.23, -30.82) * mm, "end": v(-10.98, -32.13) * mm});
            skLineSegment(sketch, "E232", {"start": v(-10.98, -32.13) * mm, "end": v(-3.81, -32.13) * mm});
            skLineSegment(sketch, "E233", {"start": v(-3.81, -32.13) * mm, "end": v(-9.45, -38.79) * mm});
            skLineSegment(sketch, "E234", {"start": v(-3.16, -34.63) * mm, "end": v(-0.98, -32.38) * mm});
            skLineSegment(sketch, "E235", {"start": v(-0.98, -32.38) * mm, "end": v(1.5, -32.38) * mm});
            skLineSegment(sketch, "E236", {"start": v(1.5, -32.38) * mm, "end": v(1.5, -40.5) * mm});
            skLineSegment(sketch, "E237", {"start": v(1.5, -40.5) * mm, "end": v(-0.23, -40.5) * mm});
            skLineSegment(sketch, "E238", {"start": v(-0.23, -40.5) * mm, "end": v(-0.23, -34.26) * mm});
            skLineSegment(sketch, "E239", {"start": v(-0.23, -34.26) * mm, "end": v(-1.81, -35.99) * mm});
            skLineSegment(sketch, "E240", {"start": v(-1.81, -35.99) * mm, "end": v(-3.16, -34.63) * mm});
            skLineSegment(sketch, "E241", {"start": v(2.64, -32.04) * mm, "end": v(2.64, -39.86) * mm});
            skLineSegment(sketch, "E242", {"start": v(2.64, -39.86) * mm, "end": v(14, -39.86) * mm});
            skLineSegment(sketch, "E243", {"start": v(14, -39.86) * mm, "end": v(14, -31.9) * mm});
            skLineSegment(sketch, "E244", {"start": v(14, -31.9) * mm, "end": v(8.77, -31.9) * mm});
            skLineSegment(sketch, "E245", {"start": v(8.77, -31.9) * mm, "end": v(6.14, -35.24) * mm});
            skLineSegment(sketch, "E246", {"start": v(6.14, -35.24) * mm, "end": v(8.24, -35.24) * mm});
            skLineSegment(sketch, "E247", {"start": v(8.24, -35.24) * mm, "end": v(9.58, -33.87) * mm});
            skLineSegment(sketch, "E248", {"start": v(9.58, -33.87) * mm, "end": v(11.85, -33.87) * mm});
            skLineSegment(sketch, "E249", {"start": v(11.85, -33.87) * mm, "end": v(11.85, -38.1) * mm});
            skLineSegment(sketch, "E250", {"start": v(11.85, -38.1) * mm, "end": v(4.6, -38.1) * mm});
            skLineSegment(sketch, "E251", {"start": v(4.6, -38.1) * mm, "end": v(4.6, -32.04) * mm});
            skLineSegment(sketch, "E252", {"start": v(4.6, -32.04) * mm, "end": v(2.64, -32.04) * mm});
            skLineSegment(sketch, "E253", {"start": v(15.45, -32.36) * mm, "end": v(23.22, -40.07) * mm});
            skLineSegment(sketch, "E254", {"start": v(23.22, -40.07) * mm, "end": v(25.71, -40.07) * mm});
            skLineSegment(sketch, "E255", {"start": v(25.71, -40.07) * mm, "end": v(25.71, -32.09) * mm});
            skLineSegment(sketch, "E256", {"start": v(25.71, -32.09) * mm, "end": v(23.43, -32.09) * mm});
            skLineSegment(sketch, "E257", {"start": v(23.43, -32.09) * mm, "end": v(23.43, -38.05) * mm});
            skLineSegment(sketch, "E258", {"start": v(23.43, -38.05) * mm, "end": v(18.11, -32.36) * mm});
            skLineSegment(sketch, "E259", {"start": v(18.11, -32.36) * mm, "end": v(15.45, -32.36) * mm});
            skLineSegment(sketch, "E260", {"start": v(14.5, -36.24) * mm, "end": v(20.66, -38.52) * mm});
            skLineSegment(sketch, "E261", {"start": v(20.66, -38.52) * mm, "end": v(20.08, -40.1) * mm});
            skLineSegment(sketch, "E262", {"start": v(20.08, -40.1) * mm, "end": v(14.4, -38) * mm});
            skLineSegment(sketch, "E263", {"start": v(14.16, -37.34) * mm, "end": v(14.5, -36.24) * mm});
            skPoint(sketch, "E264.orphan", {"position": v(-27.16, -31.65) * mm});
            skLineSegment(sketch, "E265", {"start": v(14.4, -38) * mm, "end": v(14.16, -37.34) * mm});
            skSolve(sketch);
        }
        {
            var Q0;
            Q0=makeQuery(id+"F0.imprint","IMPRINT",FACE,{"disambiguationData":[TD([[makeQuery(id+"F0.imprint","IMPRINT",EDGE,{"derivedFrom":sQuery(id+"F0.wireOp",EDGE,"E20")}),-1.0]])]});
            var Q1;
            {var subQ5=sQuery(id+"F0.wireOp",EDGE,"E2");Q1=makeQuery(id+"F0.imprint","IMPRINT",FACE,{"disambiguationData":[TD([[makeQuery(id+"F0.imprint","IMPRINT",EDGE,{"derivedFrom":subQ5}),-1.0]])]});}
            var Q2;
            Q2=makeQuery(id+"F0.imprint","IMPRINT",FACE,{"disambiguationData":[TD([[makeQuery(id+"F0.imprint","IMPRINT",EDGE,{"derivedFrom":sQuery(id+"F0.wireOp",EDGE,"E90")}),-1.0]])]});
            var Q3;
            {var subQ1=sQuery(id+"F0.wireOp",EDGE,"E7.MirrorCS");var subQ3=sQuery(id+"F0.wireOp",EDGE,"E16.MirrorCS");var subQ4=makeQuery(id+"F0.imprint","INTERSECT",VERTEX,{"derivedFrom":[subQ1,subQ3]});Q3=makeQuery(id+"F0.imprint","IMPRINT",FACE,{"disambiguationData":[TD([[makeQuery(id+"F0.imprint","IMPRINT",EDGE,{"disambiguationData":[TD([[subQ4,-1.0]])],"derivedFrom":subQ3}),-1.0]])]});}
            var Q4;
            {var subQ0=sQuery(id+"F0.wireOp",EDGE,"E14.MirrorCS");var subQ1=sQuery(id+"F0.wireOp",EDGE,"E13.MirrorCS");var subQ2=makeQuery(id+"F0.imprint","INTERSECT",VERTEX,{"derivedFrom":[subQ1,subQ0]});Q4=makeQuery(id+"F0.imprint","IMPRINT",FACE,{"disambiguationData":[TD([[makeQuery(id+"F0.imprint","IMPRINT",EDGE,{"disambiguationData":[TD([[subQ2,-1.0]])],"derivedFrom":subQ1}),1.0]])]});}
            var Q5;
            {var subQ6=sQuery(id+"F0.wireOp",EDGE,"E167");Q5=makeQuery(id+"F0.imprint","IMPRINT",FACE,{"disambiguationData":[TD([[makeQuery(id+"F0.imprint","IMPRINT",EDGE,{"derivedFrom":subQ6}),1.0]])]});}
            var Q6;
            {var subQ0=sQuery(id+"F0.wireOp",EDGE,"E169");Q6=makeQuery(id+"F0.imprint","IMPRINT",FACE,{"disambiguationData":[TD([[makeQuery(id+"F0.imprint","IMPRINT",EDGE,{"derivedFrom":subQ0}),1.0]])]});}
            var Q7;
            {var subQ14=sQuery(id+"F0.wireOp",EDGE,"E31");Q7=makeQuery(id+"F0.imprint","IMPRINT",FACE,{"disambiguationData":[TD([[makeQuery(id+"F0.imprint","IMPRINT",EDGE,{"derivedFrom":subQ14}),1.0]])]});}
            var Q8;
            Q8=makeQuery(id+"F0.imprint","IMPRINT",FACE,{"disambiguationData":[TD([[makeQuery(id+"F0.imprint","IMPRINT",EDGE,{"derivedFrom":sQuery(id+"F0.wireOp",EDGE,"E153")}),1.0]])]});
            extrude(context, id + "F1", {"entities" : qUnion([Q0, Q1, Q2, Q3, Q4, Q5, Q6, Q7, Q8]), "depth" : 25.4 * mm, "offsetDistance" : 25.4 * mm});
        }
        {
            var Q0;
            Q0=makeQuery(id+"F0.imprint","IMPRINT",FACE,{"disambiguationData":[TD([[makeQuery(id+"F0.imprint","IMPRINT",EDGE,{"derivedFrom":sQuery(id+"F0.wireOp",EDGE,"E139")}),1.0]])]});
            var Q1;
            {var subQ4=sQuery(id+"F0.wireOp",EDGE,"E128");Q1=makeQuery(id+"F0.imprint","IMPRINT",FACE,{"disambiguationData":[TD([[makeQuery(id+"F0.imprint","IMPRINT",EDGE,{"derivedFrom":subQ4}),-1.0]])]});}
            var Q2;
            Q2=makeQuery(id+"F0.imprint","IMPRINT",FACE,{"disambiguationData":[TD([[makeQuery(id+"F0.imprint","IMPRINT",EDGE,{"derivedFrom":sQuery(id+"F0.wireOp",EDGE,"E130")}),1.0]])]});
            var Q3;
            {var subQ2=sQuery(id+"F0.wireOp",EDGE,"E38");Q3=makeQuery(id+"F0.imprint","IMPRINT",FACE,{"disambiguationData":[TD([[makeQuery(id+"F0.imprint","IMPRINT",EDGE,{"derivedFrom":subQ2}),-1.0]])]});}
            extrude(context, id + "F2", {"entities" : qUnion([Q0, Q1, Q2, Q3]), "depth" : 27.94 * mm, "offsetDistance" : 25.4 * mm});
        }
        {
            var Q0;
            {var subQ0=sQuery(id+"F0.wireOp",EDGE,"E127.bottom");Q0=makeQuery(id+"F0.imprint","IMPRINT",FACE,{"disambiguationData":[TD([[makeQuery(id+"F0.imprint","IMPRINT",EDGE,{"derivedFrom":subQ0}),1.0]])]});}
            var Q1;
            {var subQ4=sQuery(id+"F0.wireOp",EDGE,"E127.right");Q1=makeQuery(id+"F0.imprint","IMPRINT",FACE,{"disambiguationData":[TD([[makeQuery(id+"F0.imprint","IMPRINT",EDGE,{"derivedFrom":subQ4}),-1.0]])]});}
            var Q2;
            Q2=makeQuery(id+"F0.imprint","IMPRINT",FACE,{"disambiguationData":[TD([[makeQuery(id+"F0.imprint","IMPRINT",EDGE,{"derivedFrom":sQuery(id+"F0.wireOp",EDGE,"E20")}),1.0]])]});
            var Q3;
            {var subQ3=sQuery(id+"F0.wireOp",EDGE,"E28");Q3=makeQuery(id+"F0.imprint","IMPRINT",FACE,{"disambiguationData":[TD([[makeQuery(id+"F0.imprint","IMPRINT",EDGE,{"derivedFrom":subQ3}),-1.0]])]});}
            var Q4;
            Q4=makeQuery(id+"F0.imprint","IMPRINT",FACE,{"disambiguationData":[TD([[makeQuery(id+"F0.imprint","IMPRINT",EDGE,{"derivedFrom":sQuery(id+"F0.wireOp",EDGE,"E117")}),-1.0]])]});
            var Q5;
            Q5=makeQuery(id+"F0.imprint","IMPRINT",FACE,{"disambiguationData":[TD([[makeQuery(id+"F0.imprint","IMPRINT",EDGE,{"derivedFrom":sQuery(id+"F0.wireOp",EDGE,"E120")}),-1.0]])]});
            var Q6;
            Q6=makeQuery(id+"F0.imprint","IMPRINT",FACE,{"disambiguationData":[TD([[makeQuery(id+"F0.imprint","IMPRINT",EDGE,{"derivedFrom":sQuery(id+"F0.wireOp",EDGE,"E102.left")}),1.0]])]});
            var Q7;
            Q7=makeQuery(id+"F0.imprint","IMPRINT",FACE,{"disambiguationData":[TD([[makeQuery(id+"F0.imprint","IMPRINT",EDGE,{"derivedFrom":sQuery(id+"F0.wireOp",EDGE,"E90")}),1.0]])]});
            var Q8;
            Q8=makeQuery(id+"F0.imprint","IMPRINT",FACE,{"disambiguationData":[TD([[makeQuery(id+"F0.imprint","IMPRINT",EDGE,{"derivedFrom":sQuery(id+"F0.wireOp",EDGE,"E111.bottom")}),1.0]])]});
            var Q9;
            Q9=makeQuery(id+"F0.imprint","IMPRINT",FACE,{"disambiguationData":[TD([[makeQuery(id+"F0.imprint","IMPRINT",EDGE,{"derivedFrom":sQuery(id+"F0.wireOp",EDGE,"E40.bottom")}),1.0]])]});
            var Q10;
            Q10=makeQuery(id+"F0.imprint","IMPRINT",FACE,{"disambiguationData":[TD([[makeQuery(id+"F0.imprint","IMPRINT",EDGE,{"derivedFrom":sQuery(id+"F0.wireOp",EDGE,"E65")}),1.0]])]});
            var Q11;
            Q11=makeQuery(id+"F0.imprint","IMPRINT",FACE,{"disambiguationData":[TD([[makeQuery(id+"F0.imprint","IMPRINT",EDGE,{"derivedFrom":sQuery(id+"F0.wireOp",EDGE,"E44")}),1.0]])]});
            var Q12;
            Q12=makeQuery(id+"F0.imprint","IMPRINT",FACE,{"disambiguationData":[TD([[makeQuery(id+"F0.imprint","IMPRINT",EDGE,{"derivedFrom":sQuery(id+"F0.wireOp",EDGE,"E42.left")}),1.0]])]});
            var Q13;
            Q13=makeQuery(id+"F0.imprint","IMPRINT",FACE,{"disambiguationData":[TD([[makeQuery(id+"F0.imprint","IMPRINT",EDGE,{"derivedFrom":sQuery(id+"F0.wireOp",EDGE,"E61")}),-1.0]])]});
            var Q14;
            Q14=makeQuery(id+"F0.imprint","IMPRINT",FACE,{"disambiguationData":[TD([[makeQuery(id+"F0.imprint","IMPRINT",EDGE,{"derivedFrom":sQuery(id+"F0.wireOp",EDGE,"E69.bottom")}),-1.0]])]});
            var Q15;
            {var subQ2=sQuery(id+"F0.wireOp",EDGE,"E76");Q15=makeQuery(id+"F0.imprint","IMPRINT",FACE,{"disambiguationData":[TD([[makeQuery(id+"F0.imprint","IMPRINT",EDGE,{"derivedFrom":subQ2}),-1.0]])]});}
            var Q16;
            Q16=makeQuery(id+"F0.imprint","IMPRINT",FACE,{"disambiguationData":[TD([[makeQuery(id+"F0.imprint","IMPRINT",EDGE,{"derivedFrom":sQuery(id+"F0.wireOp",EDGE,"E207.bottom")}),-1.0]])]});
            var Q17;
            Q17=makeQuery(id+"F0.imprint","IMPRINT",FACE,{"disambiguationData":[TD([[makeQuery(id+"F0.imprint","IMPRINT",EDGE,{"derivedFrom":sQuery(id+"F0.wireOp",EDGE,"E208.bottom")}),-1.0]])]});
            var Q18;
            {var subQ4=sQuery(id+"F0.wireOp",EDGE,"E209.bottom");Q18=makeQuery(id+"F0.imprint","IMPRINT",FACE,{"disambiguationData":[TD([[makeQuery(id+"F0.imprint","IMPRINT",EDGE,{"derivedFrom":subQ4}),-1.0]])]});}
            var Q19;
            Q19=makeQuery(id+"F0.imprint","IMPRINT",FACE,{"disambiguationData":[TD([[makeQuery(id+"F0.imprint","IMPRINT",EDGE,{"derivedFrom":sQuery(id+"F0.wireOp",EDGE,"E197")}),-1.0]])]});
            var Q20;
            Q20=makeQuery(id+"F0.imprint","IMPRINT",FACE,{"disambiguationData":[TD([[makeQuery(id+"F0.imprint","IMPRINT",EDGE,{"derivedFrom":sQuery(id+"F0.wireOp",EDGE,"E191")}),1.0]])]});
            var Q21;
            Q21=makeQuery(id+"F0.imprint","IMPRINT",FACE,{"disambiguationData":[TD([[makeQuery(id+"F0.imprint","IMPRINT",EDGE,{"derivedFrom":sQuery(id+"F0.wireOp",EDGE,"E183.MirrorCS")}),-1.0]])]});
            var Q22;
            {var subQ6=sQuery(id+"F0.wireOp",EDGE,"E167");Q22=makeQuery(id+"F0.imprint","IMPRINT",FACE,{"disambiguationData":[TD([[makeQuery(id+"F0.imprint","IMPRINT",EDGE,{"derivedFrom":subQ6}),-1.0]])]});}
            var Q23;
            Q23=makeQuery(id+"F0.imprint","IMPRINT",FACE,{"disambiguationData":[TD([[makeQuery(id+"F0.imprint","IMPRINT",EDGE,{"derivedFrom":sQuery(id+"F0.wireOp",EDGE,"E175")}),1.0]])]});
            var Q24;
            Q24=makeQuery(id+"F0.imprint","IMPRINT",FACE,{"disambiguationData":[TD([[makeQuery(id+"F0.imprint","IMPRINT",EDGE,{"derivedFrom":sQuery(id+"F0.wireOp",EDGE,"E228")}),1.0]])]});
            var Q25;
            Q25=makeQuery(id+"F0.imprint","IMPRINT",FACE,{"disambiguationData":[TD([[makeQuery(id+"F0.imprint","IMPRINT",EDGE,{"derivedFrom":sQuery(id+"F0.wireOp",EDGE,"E221")}),-1.0]])]});
            var Q26;
            {var subQ0=sQuery(id+"F0.wireOp",EDGE,"E210");Q26=makeQuery(id+"F0.imprint","IMPRINT",FACE,{"disambiguationData":[TD([[makeQuery(id+"F0.imprint","IMPRINT",EDGE,{"derivedFrom":subQ0}),1.0]])]});}
            var Q27;
            Q27=makeQuery(id+"F0.imprint","IMPRINT",FACE,{"disambiguationData":[TD([[makeQuery(id+"F0.imprint","IMPRINT",EDGE,{"derivedFrom":sQuery(id+"F0.wireOp",EDGE,"E217")}),-1.0]])]});
            var Q28;
            Q28=makeQuery(id+"F0.imprint","IMPRINT",FACE,{"disambiguationData":[TD([[makeQuery(id+"F0.imprint","IMPRINT",EDGE,{"derivedFrom":sQuery(id+"F0.wireOp",EDGE,"E234")}),-1.0]])]});
            var Q29;
            Q29=makeQuery(id+"F0.imprint","IMPRINT",FACE,{"disambiguationData":[TD([[makeQuery(id+"F0.imprint","IMPRINT",EDGE,{"derivedFrom":sQuery(id+"F0.wireOp",EDGE,"E241")}),1.0]])]});
            var Q30;
            Q30=makeQuery(id+"F0.imprint","IMPRINT",FACE,{"disambiguationData":[TD([[makeQuery(id+"F0.imprint","IMPRINT",EDGE,{"derivedFrom":sQuery(id+"F0.wireOp",EDGE,"E260")}),-1.0]])]});
            var Q31;
            {var subQ0=sQuery(id+"F0.wireOp",EDGE,"E253");Q31=makeQuery(id+"F0.imprint","IMPRINT",FACE,{"disambiguationData":[TD([[makeQuery(id+"F0.imprint","IMPRINT",EDGE,{"derivedFrom":subQ0}),1.0]])]});}
            var Q32;
            {var subQ0=sQuery(id+"F0.wireOp",EDGE,"E127.left");Q32=makeQuery(id+"F0.imprint","IMPRINT",FACE,{"disambiguationData":[TD([[makeQuery(id+"F0.imprint","IMPRINT",EDGE,{"derivedFrom":subQ0}),1.0]])]});}
            extrude(context, id + "F3", {"entities" : qUnion([Q0, Q1, Q2, Q3, Q4, Q5, Q6, Q7, Q8, Q9, Q10, Q11, Q12, Q13, Q14, Q15, Q16, Q17, Q18, Q19, Q20, Q21, Q22, Q23, Q24, Q25, Q26, Q27, Q28, Q29, Q30, Q31, Q32]), "depth" : 30.48 * mm, "offsetDistance" : 25.4 * mm});
        }
    });
